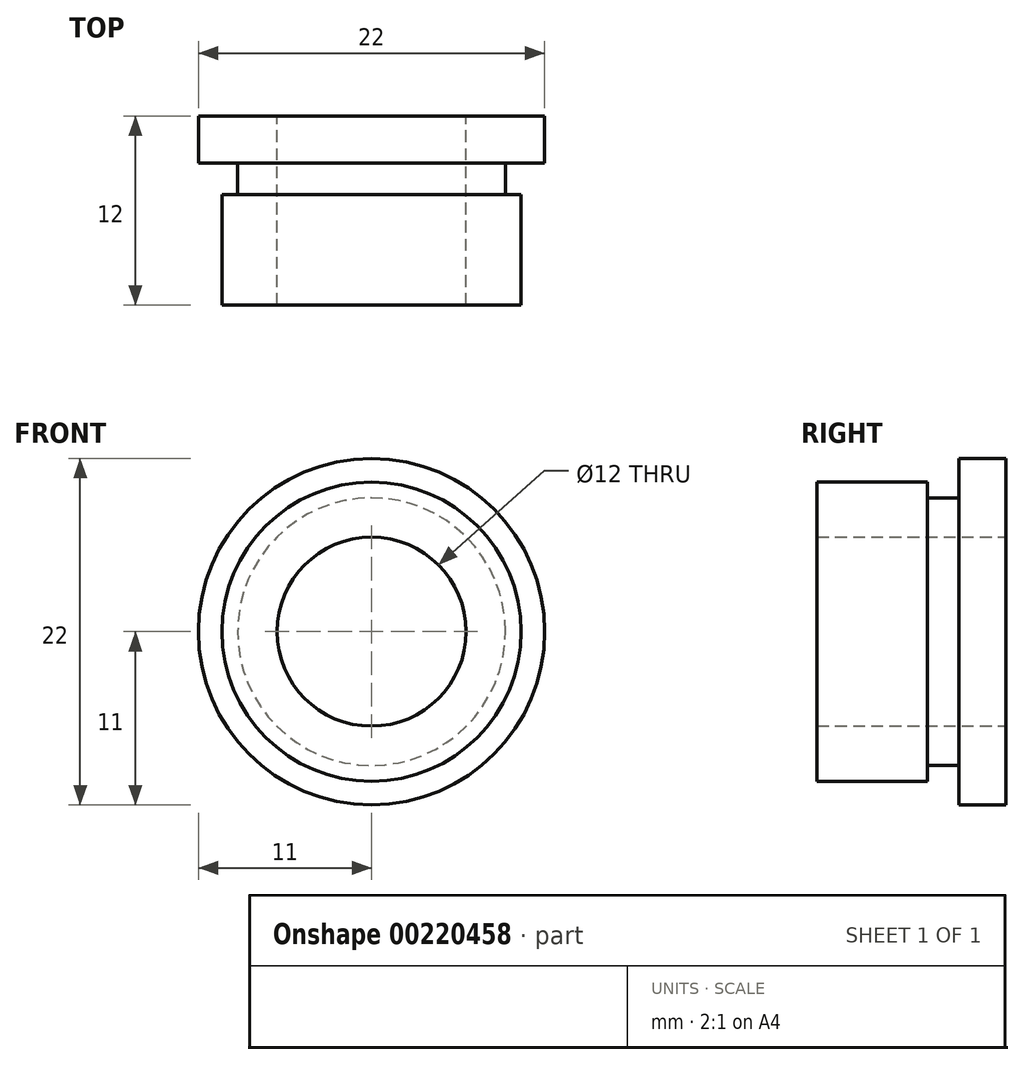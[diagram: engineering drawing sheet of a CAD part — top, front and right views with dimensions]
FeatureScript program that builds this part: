
annotation { "Feature Type Name" : "Feature", "Feature Type Description" : "" }
export const myFeature = defineFeature(function(context is Context, id is Id, definition is map)
    precondition{}
    {
        {
            var Q0;
            Q0=qCreatedBy(makeId("Front.planeOp"),FACE);
            var sketch = newSketch(context, id + "F0", { "sketchPlane" : qUnion([Q0])});
            skCircle(sketch, "E0", {"center": v(0, 0) * mm, "radius": 6 * mm});
            skCircle(sketch, "E1", {"center": v(0, 0) * mm, "radius": 9.5 * mm});
            skSolve(sketch);
        }
        {
            var Q0;
            Q0=makeQuery(id+"F0.imprint","IMPRINT",FACE,{"disambiguationData":[TD([[makeQuery(id+"F0.imprint","IMPRINT",EDGE,{"derivedFrom":sQuery(id+"F0.wireOp",EDGE,"E0")}),-1.0]])]});
            extrude(context, id + "F1", {"entities" : qUnion([Q0]), "depth" : 7 * mm});
        }
        {
            var Q0;
            Q0=qCreatedBy(makeId("Front.planeOp"),FACE);
            var sketch = newSketch(context, id + "F2", { "sketchPlane" : qUnion([Q0])});
            skCircle(sketch, "E2", {"center": v(0, 0) * mm, "radius": 6 * mm});
            skCircle(sketch, "E3", {"center": v(0, 0) * mm, "radius": 8.5 * mm});
            skSolve(sketch);
        }
        {
            var Q0;
            Q0 = qSketchRegion(id + "F2", true);
            extrude(context, id + "F3", {"entities" : qUnion([Q0]), "operationType" : NewBodyOperationType.ADD, "oppositeDirection" : true, "depth" : 2 * mm});
        }
        {
            var Q0;
            Q0=makeQuery(id+"F3.opExtrude","CAP_FACE",FACE,{"disambiguationData":[OSD([sQuery(id+"F2.wireOp",EDGE,"E2"),sQuery(id+"F2.wireOp",EDGE,"E3")])],"isStart":false});
            var sketch = newSketch(context, id + "F4", { "sketchPlane" : qUnion([Q0])});
            skCircle(sketch, "E4", {"center": v(0, 0) * mm, "radius": 6 * mm});
            skCircle(sketch, "E5", {"center": v(0, 0) * mm, "radius": 11 * mm});
            skSolve(sketch);
        }
        {
            var Q0;
            Q0=makeQuery(id+"F4.imprint","IMPRINT",FACE,{"disambiguationData":[TD([[makeQuery(id+"F4.imprint","IMPRINT",EDGE,{"derivedFrom":sQuery(id+"F4.wireOp",EDGE,"E4")}),1.0]])]});
            var Q1;
            Q1=makeQuery(id+"F4.imprint","IMPRINT",FACE,{"disambiguationData":[TD([[makeQuery(id+"F4.imprint","IMPRINT",EDGE,{"derivedFrom":sQuery(id+"F4.wireOp",EDGE,"E5")}),1.0]])]});
            extrude(context, id + "F5", {"entities" : qUnion([Q0, Q1]), "operationType" : NewBodyOperationType.ADD, "depth" : 3 * mm});
        }
    });
